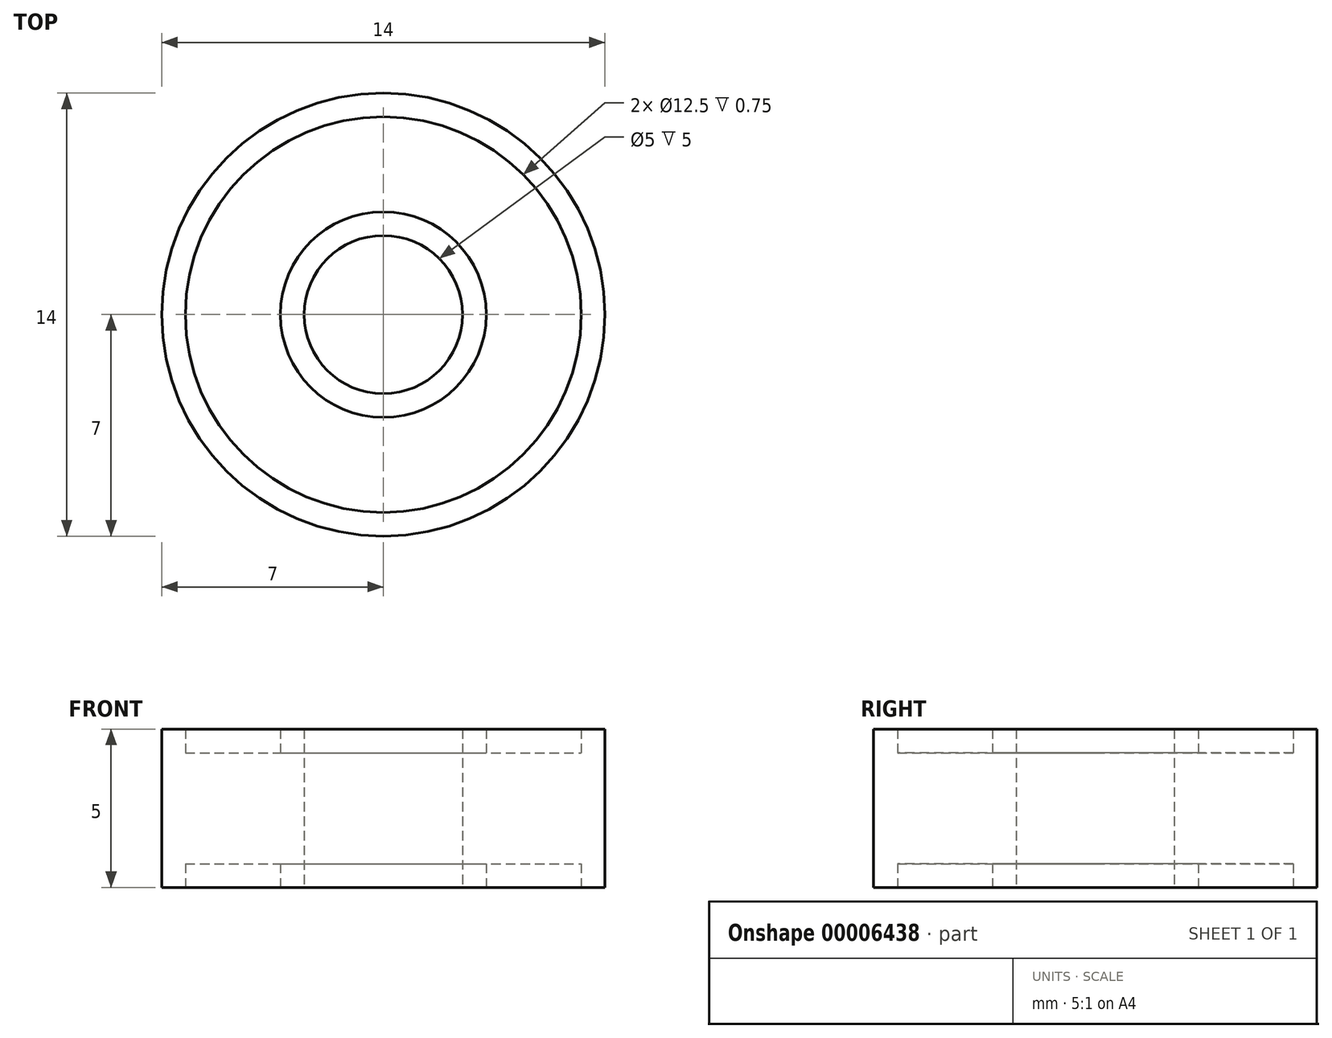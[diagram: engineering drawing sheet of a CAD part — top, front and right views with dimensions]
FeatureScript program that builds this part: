
annotation { "Feature Type Name" : "Feature", "Feature Type Description" : "" }
export const myFeature = defineFeature(function(context is Context, id is Id, definition is map)
    precondition{}
    {
        {
            var Q0;
            Q0=qCreatedBy(makeId("Front.planeOp"),FACE);
            var sketch = newSketch(context, id + "F0", { "sketchPlane" : qUnion([Q0])});
            skLineSegment(sketch, "E0", {"start": v(-2.5, 0) * mm, "end": v(-2.5, 2.5) * mm});
            skLineSegment(sketch, "E1", {"start": v(-2.5, 2.5) * mm, "end": v(-3.25, 2.5) * mm});
            skLineSegment(sketch, "E2", {"start": v(-3.25, 2.5) * mm, "end": v(-3.25, 1.75) * mm});
            skLineSegment(sketch, "E3", {"start": v(-3.25, 1.75) * mm, "end": v(-6.25, 1.75) * mm});
            skLineSegment(sketch, "E4", {"start": v(-6.25, 1.75) * mm, "end": v(-6.25, 2.5) * mm});
            skLineSegment(sketch, "E5", {"start": v(-6.25, 2.5) * mm, "end": v(-7, 2.5) * mm});
            skLineSegment(sketch, "E6", {"start": v(-7, 2.5) * mm, "end": v(-7, 0) * mm});
            skLineSegment(sketch, "E7", {"start": v(-6.25, 2.5) * mm, "end": v(-3.25, 2.5) * mm, "construction": true});
            skLineSegment(sketch, "E8.0.MirrorCS", {"start": v(-2.5, 0) * mm, "end": v(-2.5, -2.5) * mm});
            skLineSegment(sketch, "E8.1.MirrorCS", {"start": v(-3.25, -2.5) * mm, "end": v(-3.25, -1.75) * mm});
            skLineSegment(sketch, "E8.2.MirrorCS", {"start": v(-3.25, -1.75) * mm, "end": v(-6.25, -1.75) * mm});
            skLineSegment(sketch, "E8.3.MirrorCS", {"start": v(-7, -2.5) * mm, "end": v(-7, 0) * mm});
            skLineSegment(sketch, "E8.4.MirrorCS", {"start": v(-6.25, -2.5) * mm, "end": v(-7, -2.5) * mm});
            skLineSegment(sketch, "E8.5.MirrorCS", {"start": v(-6.25, -1.75) * mm, "end": v(-6.25, -2.5) * mm});
            skLineSegment(sketch, "E8.6.MirrorCS", {"start": v(-6.25, -2.5) * mm, "end": v(-3.25, -2.5) * mm, "construction": true});
            skLineSegment(sketch, "E8.7.MirrorCS", {"start": v(-2.5, -2.5) * mm, "end": v(-3.25, -2.5) * mm});
            skLineSegment(sketch, "E9", {"start": v(0, 0) * mm, "end": v(0, 4.98) * mm, "construction": true});
            skSolve(sketch);
        }
        {
            var Q0;
            Q0=makeQuery(id+"F0.imprint","IMPRINT",FACE,{"disambiguationData":[TD([[makeQuery(id+"F0.imprint","IMPRINT",EDGE,{"derivedFrom":sQuery(id+"F0.wireOp",EDGE,"E0")}),1.0]])]});
            var Q1;
            Q1=sQuery(id+"F0.wireOp",EDGE,"E9");
            revolve(context, id + "F1", {"entities" : qUnion([Q0]), "axis" : qUnion([Q1]), "revolveType" : RevolveType.FULL});
        }
    });
